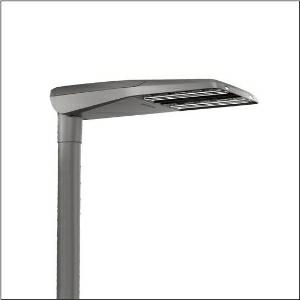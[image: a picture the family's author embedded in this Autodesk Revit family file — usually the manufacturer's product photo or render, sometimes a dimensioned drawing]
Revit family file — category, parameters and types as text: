
# Revit family: streetlight_sl_11_iq_midi___st1_0ab_5xc3n51f08me_d360
name_source: partatom
category: Lighting Fixtures
units: mm (PartAtom-declared; Revit-internal decimal feet)

## family parameters
Cut with Voids When Loaded = No
Host = Face
Light Source = No
Part Type = Normal
Room Calculation Point = No
Round Connector Dimension = Use Diameter
Shared = No

## types (1)
- --- (1 x LED, 15260 lm, 124.7 W, 3000K)
    Apparent Load = 125 VA
    CIE Flux Codes = 29 63 95 100 100
    Color Rendering = 70
    Color Temperature = 3000K
    Default Elevation = 1800 mm
    Description = Streetlight SL 11 iQ midi, mast luminaire, primary light control with 3 zone facetted reflector, of plastic, silver coated, highly specular, primary optical cover: cover, of PMMA, transparent, light distribution: ST1.0aB, light emission: direct distribution, primary light characteristic: asymmetric, installation type: post-top, side-entry, lamps: LED, High Power LED, rated values: 15.260lm | 124,7W | 122,4lm/W (begin service life); end service life: 15.260lm | 132,2W; at 50% lumin. flux: 7.630lm | 57,2W | 133,4lm/W, colour temperature: 3000K, colour rendering: CRI > 70, light colour: 730, light setting 1 begin service life: 100% | 15.260lm | 124,7W | 122,4lm/W | 3.000K, light setting 1 end service life: 132,2W, further light settings possible, control: optimised constant luminous flux control (CLO 2.0), Street-Remote, Desk-Remote (wireless, voltage-free reading and setting of iQ features in the workshop via application-optimized NFC function/RFID function), Light-Fading, Smart-Wire, Night-Set, Lumen-Switch, Temp-Guard, Auto-Match, with cable H07RN-F 5x 1.5mm², mains connection: 230..240V, AC, 50/60Hz, connection cable pre-assembled, cable length: 12,5m, luminaire housing, of diecast aluminium, powder-coated, Siteco® metallic grey (DB 702S), please order mast flange separately, inclination adjustable without tools: 0°, 5°, 10°, 15° (post-top) | 0°, -5°, -10°, -15° (side-entry), sealing non-destructively replaceable, multi-level sealing system, length: 780mm, width: 376mm, height: 118mm, mast flange for spigot size: 42mm (side-entry): 5XC10008XM4, 60/48mm (side-entry/post-top): 5XC10108XM2, 76/60mm (side-entry/post-top): 5XC10108XM1, equipment: Power, protection rating (complete): IP66, insulation class (complete): insulation class II (safety insulation), certification: CE, ENEC, ENEC+, VDE, impact resistance: IK10, permissible operating ambient temperature for outdoor applications: -25..+50°C, standard-compliant lighting for roads and squares, Environmental Product Declaration (EPD) tested and certified by an independent institute, packaging unit: 1 piece

Light Distribution: ST1.0aB
    Height = 118 mm
    Lamp = 1 x LED
    Lamp Light Flux = 15260 lm
    Lamp Power = 124.7 W
    Lamp count = 1
    Length = 780 mm
    Luminous efficacy = 122 lm/W
    Manufacturer = Siteco
    ModVariant = No
    Model = 5XC3N51F08ME
    Number of Poles = 1
    OnlyDefault = Yes
    Power Factor = 1
    Product Name = Streetlight SL 11 iQ midi | ST1.0aB
    Product group = mast luminaire | pylon top
    ProductGroupID = 6100
    Protection Class = Protection class II
    Protection Degree = IP 66
    RLX_Detail_Level = 1
    RLX_Emergency_Light_Flux = 0 lm
    RLX_Emergency_Type = 0
    RLX_Emergency_Type_DB = No
    RlxData = <blob elided: 70425 chars, md5=3cae6dc0>
    Socket = socket
    Standby Power = 0 W
    System Light Flux = 15260 lm
    System Power = 125 W
    Type Comments = factory setting: luminous flux: 100 % | dim-lin: 254 | 557 mA
    Type Image = l_1005960.jpg
    URL = http://relux.com
    VarID = @adj_109447
    Voltage = 0 V
    Weight = 0.00 kg
    Width = 376 mm

## geometry (parser evidence)
native form markers: Blend x4, Sweep x9
no freeform markers — native parametric forms only
